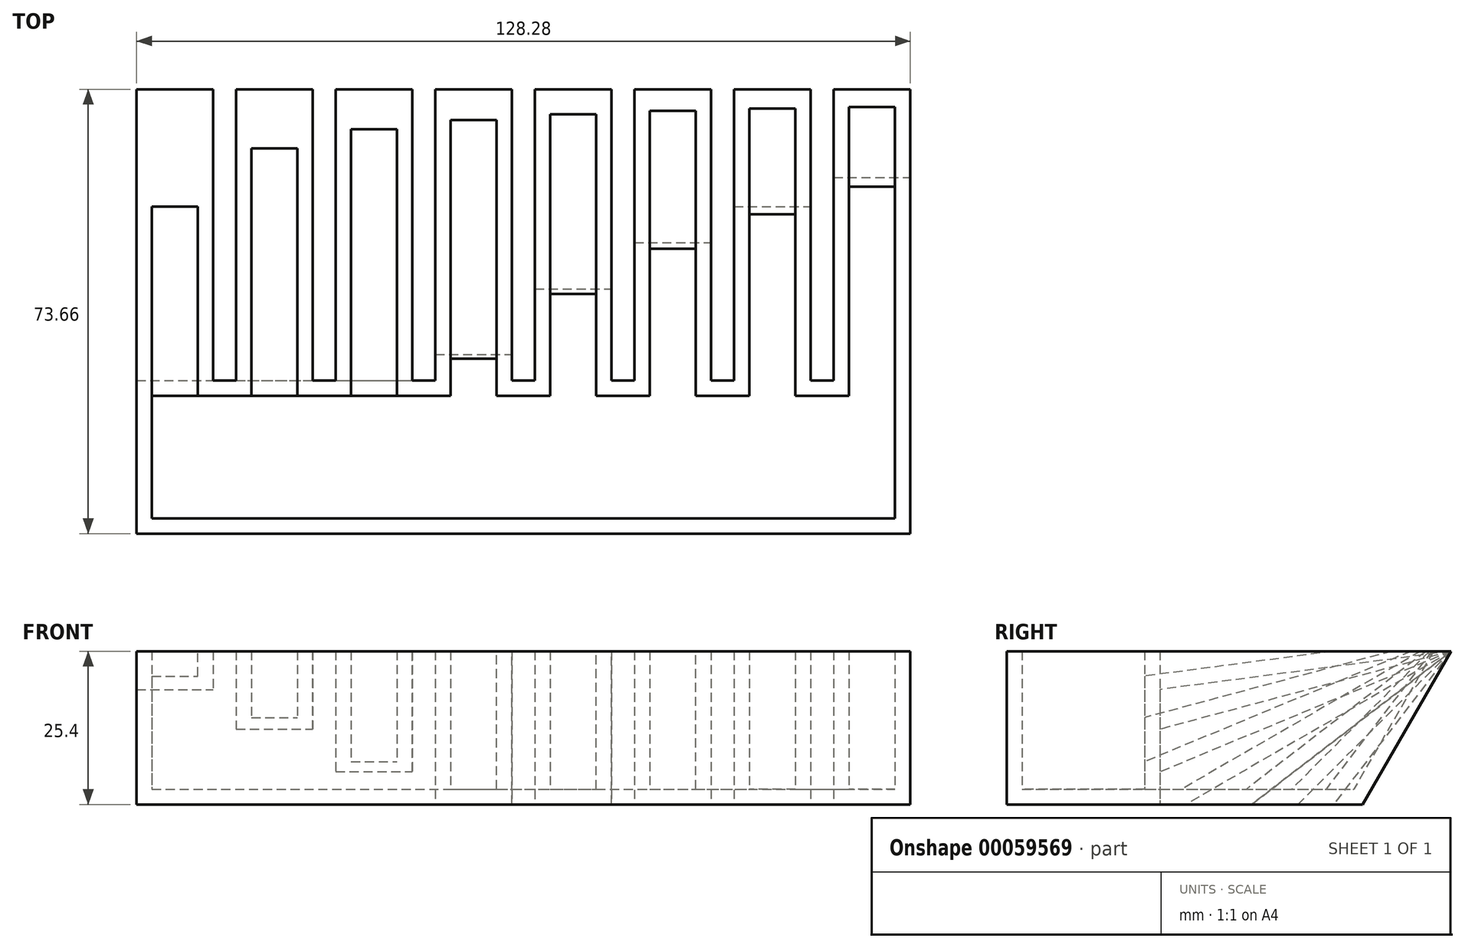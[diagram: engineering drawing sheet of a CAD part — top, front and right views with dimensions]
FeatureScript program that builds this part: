
annotation { "Feature Type Name" : "Feature", "Feature Type Description" : "" }
export const myFeature = defineFeature(function(context is Context, id is Id, definition is map)
    precondition{}
    {
        {
            var Q0;
            Q0=qCreatedBy(makeId("Top.planeOp"),FACE);
            var sketch = newSketch(context, id + "F0", { "sketchPlane" : qUnion([Q0])});
            skLineSegment(sketch, "E0.bottom", {"start": v(-97.16, 0) * mm, "end": v(-84.46, 0) * mm});
            skLineSegment(sketch, "E0.top", {"start": v(-97.16, 50.8) * mm, "end": v(-84.46, 50.8) * mm});
            skLineSegment(sketch, "E0.left", {"start": v(-97.16, 0) * mm, "end": v(-97.16, 50.8) * mm});
            skLineSegment(sketch, "E0.right", {"start": v(-84.46, 0) * mm, "end": v(-84.46, 50.8) * mm});
            skLineSegment(sketch, "E1.bottom", {"start": v(-64.14, 0) * mm, "end": v(-51.44, 0) * mm});
            skLineSegment(sketch, "E1.top", {"start": v(-64.14, 50.8) * mm, "end": v(-51.44, 50.8) * mm});
            skLineSegment(sketch, "E1.left", {"start": v(-64.14, 0) * mm, "end": v(-64.14, 50.8) * mm});
            skLineSegment(sketch, "E1.right", {"start": v(-51.44, 0) * mm, "end": v(-51.44, 50.8) * mm});
            skLineSegment(sketch, "E2.bottom", {"start": v(-47.63, 0) * mm, "end": v(-34.93, 0) * mm});
            skLineSegment(sketch, "E2.top", {"start": v(-47.63, 50.8) * mm, "end": v(-34.93, 50.8) * mm});
            skLineSegment(sketch, "E2.left", {"start": v(-47.63, 0) * mm, "end": v(-47.63, 50.8) * mm});
            skLineSegment(sketch, "E2.right", {"start": v(-34.93, 0) * mm, "end": v(-34.93, 50.8) * mm});
            skLineSegment(sketch, "E3.bottom", {"start": v(-80.65, 0) * mm, "end": v(-67.95, 0) * mm});
            skLineSegment(sketch, "E3.top", {"start": v(-80.65, 50.8) * mm, "end": v(-67.95, 50.8) * mm});
            skLineSegment(sketch, "E3.left", {"start": v(-80.65, 0) * mm, "end": v(-80.65, 50.8) * mm});
            skLineSegment(sketch, "E3.right", {"start": v(-67.95, 0) * mm, "end": v(-67.95, 50.8) * mm});
            skLineSegment(sketch, "E4.bottom", {"start": v(-31.12, 0) * mm, "end": v(-18.42, 0) * mm});
            skLineSegment(sketch, "E4.top", {"start": v(-31.12, 50.8) * mm, "end": v(-18.42, 50.8) * mm});
            skLineSegment(sketch, "E4.left", {"start": v(-31.12, 0) * mm, "end": v(-31.12, 50.8) * mm});
            skLineSegment(sketch, "E4.right", {"start": v(-18.42, 0) * mm, "end": v(-18.42, 50.8) * mm});
            skLineSegment(sketch, "E5.bottom", {"start": v(-14.6, 0) * mm, "end": v(-1.9, 0) * mm});
            skLineSegment(sketch, "E5.top", {"start": v(-14.6, 50.8) * mm, "end": v(-1.9, 50.8) * mm});
            skLineSegment(sketch, "E5.left", {"start": v(-14.6, 0) * mm, "end": v(-14.6, 50.8) * mm});
            skLineSegment(sketch, "E5.right", {"start": v(-1.9, 0) * mm, "end": v(-1.9, 50.8) * mm});
            skLineSegment(sketch, "E6.MirrorCS", {"start": v(31.12, 0) * mm, "end": v(31.12, 50.8) * mm});
            skLineSegment(sketch, "E7.MirrorCS", {"start": v(18.42, 0) * mm, "end": v(18.42, 50.8) * mm});
            skLineSegment(sketch, "E8.MirrorCS", {"start": v(14.6, 0) * mm, "end": v(14.6, 50.8) * mm});
            skLineSegment(sketch, "E9.MirrorCS", {"start": v(1.9, 0) * mm, "end": v(1.9, 50.8) * mm});
            skLineSegment(sketch, "E10.MirrorCS", {"start": v(14.6, 0) * mm, "end": v(1.9, 0) * mm});
            skLineSegment(sketch, "E11.MirrorCS", {"start": v(31.12, 0) * mm, "end": v(18.42, 0) * mm});
            skLineSegment(sketch, "E12.MirrorCS", {"start": v(31.12, 50.8) * mm, "end": v(18.42, 50.8) * mm});
            skLineSegment(sketch, "E13.MirrorCS", {"start": v(14.6, 50.8) * mm, "end": v(1.9, 50.8) * mm});
            skSolve(sketch);
        }
        {
            var Q0;
            Q0=makeQuery(id+"F0.imprint","IMPRINT",FACE,{"disambiguationData":[TD([[makeQuery(id+"F0.imprint","IMPRINT",EDGE,{"derivedFrom":sQuery(id+"F0.wireOp",EDGE,"E0.bottom")}),1.0]])]});
            var Q1;
            Q1=makeQuery(id+"F0.imprint","IMPRINT",FACE,{"disambiguationData":[TD([[makeQuery(id+"F0.imprint","IMPRINT",EDGE,{"derivedFrom":sQuery(id+"F0.wireOp",EDGE,"E3.bottom")}),1.0]])]});
            var Q2;
            Q2=makeQuery(id+"F0.imprint","IMPRINT",FACE,{"disambiguationData":[TD([[makeQuery(id+"F0.imprint","IMPRINT",EDGE,{"derivedFrom":sQuery(id+"F0.wireOp",EDGE,"E1.bottom")}),1.0]])]});
            var Q3;
            Q3=makeQuery(id+"F0.imprint","IMPRINT",FACE,{"disambiguationData":[TD([[makeQuery(id+"F0.imprint","IMPRINT",EDGE,{"derivedFrom":sQuery(id+"F0.wireOp",EDGE,"E2.bottom")}),1.0]])]});
            var Q4;
            Q4=makeQuery(id+"F0.imprint","IMPRINT",FACE,{"disambiguationData":[TD([[makeQuery(id+"F0.imprint","IMPRINT",EDGE,{"derivedFrom":sQuery(id+"F0.wireOp",EDGE,"E4.bottom")}),1.0]])]});
            var Q5;
            Q5=makeQuery(id+"F0.imprint","IMPRINT",FACE,{"disambiguationData":[TD([[makeQuery(id+"F0.imprint","IMPRINT",EDGE,{"derivedFrom":sQuery(id+"F0.wireOp",EDGE,"E5.bottom")}),1.0]])]});
            var Q6;
            Q6=makeQuery(id+"F0.imprint","IMPRINT",FACE,{"disambiguationData":[TD([[makeQuery(id+"F0.imprint","IMPRINT",EDGE,{"derivedFrom":sQuery(id+"F0.wireOp",EDGE,"E8.MirrorCS")}),1.0]])]});
            var Q7;
            Q7=makeQuery(id+"F0.imprint","IMPRINT",FACE,{"disambiguationData":[TD([[makeQuery(id+"F0.imprint","IMPRINT",EDGE,{"derivedFrom":sQuery(id+"F0.wireOp",EDGE,"E6.MirrorCS")}),1.0]])]});
            var Q8;
            Q8=makeQuery(id+"F0.imprint","IMPRINT",FACE,{"disambiguationData":[TD([[makeQuery(id+"F0.imprint","IMPRINT",EDGE,{"derivedFrom":sQuery(id+"F0.wireOp",EDGE,"c19ff177-619e-41c1-baba-1ab0cc4251760.MirrorCS")}),1.0]])]});
            var Q9;
            Q9=makeQuery(id+"F0.imprint","IMPRINT",FACE,{"disambiguationData":[TD([[makeQuery(id+"F0.imprint","IMPRINT",EDGE,{"derivedFrom":sQuery(id+"F0.wireOp",EDGE,"cd565e26-b1c7-4797-8e50-3720e60893980.MirrorCS")}),-1.0]])]});
            var Q10;
            Q10=makeQuery(id+"F0.imprint","IMPRINT",FACE,{"disambiguationData":[TD([[makeQuery(id+"F0.imprint","IMPRINT",EDGE,{"derivedFrom":sQuery(id+"F0.wireOp",EDGE,"f834d962-6a61-4322-8373-423d23230d6e0.MirrorCS")}),1.0]])]});
            var Q11;
            Q11=makeQuery(id+"F0.imprint","IMPRINT",FACE,{"disambiguationData":[TD([[makeQuery(id+"F0.imprint","IMPRINT",EDGE,{"derivedFrom":sQuery(id+"F0.wireOp",EDGE,"851a8a81-0ea1-476b-88e9-f5545ef320b30.MirrorCS")}),-1.0]])]});
            extrude(context, id + "F1", {"entities" : qUnion([Q0, Q1, Q2, Q3, Q4, Q5, Q6, Q7, Q8, Q9, Q10, Q11]), "depth" : 25.4 * mm});
        }
        {
            var Q0;
            Q0=makeQuery(id+"F1.opExtrude","CAP_EDGE",EDGE,{"disambiguationData":[OSD([sQuery(id+"F0.wireOp",EDGE,"E0.top")])],"isStart":true});
            chamfer(context, id + "F2", {"entities" : qUnion([Q0]), "chamferType" : ChamferType.OFFSET_ANGLE, "width" : 192.94 * mm, "oppositeDirection" : false, "angle" : 7.5 * degree, "tangentPropagation" : true});
        }
        {
            var Q0;
            Q0=makeQuery(id+"F1.opExtrude","CAP_EDGE",EDGE,{"disambiguationData":[OSD([sQuery(id+"F0.wireOp",EDGE,"E3.top")])],"isStart":true});
            chamfer(context, id + "F3", {"entities" : qUnion([Q0]), "chamferType" : ChamferType.OFFSET_ANGLE, "width" : 94.8 * mm, "oppositeDirection" : false, "angle" : 15 * degree, "tangentPropagation" : true});
        }
        {
            var Q0;
            Q0=makeQuery(id+"F1.opExtrude","CAP_EDGE",EDGE,{"disambiguationData":[OSD([sQuery(id+"F0.wireOp",EDGE,"E1.top")])],"isStart":true});
            chamfer(context, id + "F4", {"entities" : qUnion([Q0]), "chamferType" : ChamferType.OFFSET_ANGLE, "width" : 61.32 * mm, "oppositeDirection" : false, "angle" : 22.5 * degree, "tangentPropagation" : true});
        }
        {
            var Q0;
            Q0=makeQuery(id+"F1.opExtrude","CAP_EDGE",EDGE,{"disambiguationData":[OSD([sQuery(id+"F0.wireOp",EDGE,"E2.top")])],"isStart":true});
            chamfer(context, id + "F5", {"entities" : qUnion([Q0]), "chamferType" : ChamferType.OFFSET_ANGLE, "width" : 44 * mm, "oppositeDirection" : false, "angle" : 30 * degree, "tangentPropagation" : true});
        }
        {
            var Q0;
            Q0=makeQuery(id+"F1.opExtrude","CAP_EDGE",EDGE,{"disambiguationData":[OSD([sQuery(id+"F0.wireOp",EDGE,"E4.top")])],"isStart":true});
            chamfer(context, id + "F6", {"entities" : qUnion([Q0]), "chamferType" : ChamferType.OFFSET_ANGLE, "width" : 33.1 * mm, "oppositeDirection" : false, "angle" : 37.5 * degree, "tangentPropagation" : true});
        }
        {
            var Q0;
            Q0=makeQuery(id+"F1.opExtrude","CAP_EDGE",EDGE,{"disambiguationData":[OSD([sQuery(id+"F0.wireOp",EDGE,"E5.top")])],"isStart":true});
            chamfer(context, id + "F7", {"entities" : qUnion([Q0]), "chamferType" : ChamferType.OFFSET_ANGLE, "width" : 25.4 * mm, "oppositeDirection" : false, "angle" : 45 * degree, "tangentPropagation" : true});
        }
        {
            var Q0;
            Q0=makeQuery(id+"F1.opExtrude","CAP_EDGE",EDGE,{"disambiguationData":[OSD([sQuery(id+"F0.wireOp",EDGE,"E13.MirrorCS")])],"isStart":true});
            chamfer(context, id + "F8", {"entities" : qUnion([Q0]), "chamferType" : ChamferType.OFFSET_ANGLE, "width" : 25.4 * mm, "oppositeDirection" : false, "angle" : 37.5 * degree, "tangentPropagation" : true});
        }
        {
            var Q0;
            Q0=makeQuery(id+"F1.opExtrude","CAP_EDGE",EDGE,{"disambiguationData":[OSD([sQuery(id+"F0.wireOp",EDGE,"E12.MirrorCS")])],"isStart":true});
            chamfer(context, id + "F9", {"entities" : qUnion([Q0]), "chamferType" : ChamferType.OFFSET_ANGLE, "width" : 25.4 * mm, "oppositeDirection" : false, "angle" : 30 * degree, "tangentPropagation" : true});
        }
        {
            var Q0;
            Q0=qCreatedBy(makeId("Top.planeOp"),FACE);
            var sketch = newSketch(context, id + "F10", { "sketchPlane" : qUnion([Q0])});
            skLineSegment(sketch, "E14.bottom", {"start": v(-97.15, 2.54) * mm, "end": v(31.12, 2.54) * mm});
            skLineSegment(sketch, "E14.top", {"start": v(-97.15, -22.86) * mm, "end": v(31.12, -22.86) * mm});
            skLineSegment(sketch, "E14.left", {"start": v(-97.15, 2.54) * mm, "end": v(-97.15, -22.86) * mm});
            skLineSegment(sketch, "E14.right", {"start": v(31.12, 2.54) * mm, "end": v(31.12, -22.86) * mm});
            skPoint(sketch, "E15.start.orphan", {"position": v(-33.02, -22.86) * mm});
            skSolve(sketch);
        }
        {
            var Q0;
            Q0=makeQuery(id+"F10.imprint","IMPRINT",FACE,{"disambiguationData":[TD([[makeQuery(id+"F10.imprint","IMPRINT",EDGE,{"derivedFrom":sQuery(id+"F10.wireOp",EDGE,"E14.bottom")}),-1.0]])]});
            extrude(context, id + "F11", {"entities" : qUnion([Q0]), "operationType" : NewBodyOperationType.ADD, "depth" : 25.4 * mm});
        }
        {
            var Q0;
            Q0=makeQuery(id+"F11.boolean.opBoolean","MERGE",FACE,{"derivedFrom":[makeQuery(id+"F1.opExtrude","CAP_FACE",FACE,{"disambiguationData":[OSD([sQuery(id+"F0.wireOp",EDGE,"E1.bottom"),sQuery(id+"F0.wireOp",EDGE,"E1.top"),sQuery(id+"F0.wireOp",EDGE,"E1.left"),sQuery(id+"F0.wireOp",EDGE,"E1.right")])],"isStart":false}),makeQuery(id+"F1.opExtrude","CAP_FACE",FACE,{"disambiguationData":[OSD([sQuery(id+"F0.wireOp",EDGE,"E2.bottom"),sQuery(id+"F0.wireOp",EDGE,"E2.top"),sQuery(id+"F0.wireOp",EDGE,"E2.left"),sQuery(id+"F0.wireOp",EDGE,"E2.right")])],"isStart":false}),makeQuery(id+"F1.opExtrude","CAP_FACE",FACE,{"disambiguationData":[OSD([sQuery(id+"F0.wireOp",EDGE,"E3.bottom"),sQuery(id+"F0.wireOp",EDGE,"E3.top"),sQuery(id+"F0.wireOp",EDGE,"E3.left"),sQuery(id+"F0.wireOp",EDGE,"E3.right")])],"isStart":false}),makeQuery(id+"F1.opExtrude","CAP_FACE",FACE,{"disambiguationData":[OSD([sQuery(id+"F0.wireOp",EDGE,"E4.bottom"),sQuery(id+"F0.wireOp",EDGE,"E4.top"),sQuery(id+"F0.wireOp",EDGE,"E4.left"),sQuery(id+"F0.wireOp",EDGE,"E4.right")])],"isStart":false}),makeQuery(id+"F1.opExtrude","CAP_FACE",FACE,{"disambiguationData":[OSD([sQuery(id+"F0.wireOp",EDGE,"E5.bottom"),sQuery(id+"F0.wireOp",EDGE,"E5.top"),sQuery(id+"F0.wireOp",EDGE,"E5.left"),sQuery(id+"F0.wireOp",EDGE,"E5.right")])],"isStart":false}),makeQuery(id+"F1.opExtrude","CAP_FACE",FACE,{"disambiguationData":[OSD([sQuery(id+"F0.wireOp",EDGE,"cd565e26-b1c7-4797-8e50-3720e60893980.MirrorCS"),sQuery(id+"F0.wireOp",EDGE,"9d3064da-bae2-45b4-9700-95b410362f340.MirrorCS"),sQuery(id+"F0.wireOp",EDGE,"2c093ff5-e38e-4e6b-805d-5ac065703b640.MirrorCS"),sQuery(id+"F0.wireOp",EDGE,"c8e67260-9b63-45b2-a96e-6140a1e5b8520.MirrorCS")])],"isStart":false}),makeQuery(id+"F1.opExtrude","CAP_FACE",FACE,{"disambiguationData":[OSD([sQuery(id+"F0.wireOp",EDGE,"c19ff177-619e-41c1-baba-1ab0cc4251760.MirrorCS"),sQuery(id+"F0.wireOp",EDGE,"edb2ae44-dfd0-438d-9011-fcfcb738fec00.MirrorCS"),sQuery(id+"F0.wireOp",EDGE,"91fa4f69-d6ec-41a8-b3b4-15e805d021af0.MirrorCS"),sQuery(id+"F0.wireOp",EDGE,"9a140606-8439-4793-9d1a-0ec345cc02ee0.MirrorCS")])],"isStart":false}),makeQuery(id+"F1.opExtrude","CAP_FACE",FACE,{"disambiguationData":[OSD([sQuery(id+"F0.wireOp",EDGE,"E6.MirrorCS"),sQuery(id+"F0.wireOp",EDGE,"E7.MirrorCS"),sQuery(id+"F0.wireOp",EDGE,"E11.MirrorCS"),sQuery(id+"F0.wireOp",EDGE,"E12.MirrorCS")])],"isStart":false}),makeQuery(id+"F1.opExtrude","CAP_FACE",FACE,{"disambiguationData":[OSD([sQuery(id+"F0.wireOp",EDGE,"E8.MirrorCS"),sQuery(id+"F0.wireOp",EDGE,"E9.MirrorCS"),sQuery(id+"F0.wireOp",EDGE,"E10.MirrorCS"),sQuery(id+"F0.wireOp",EDGE,"E13.MirrorCS")])],"isStart":false}),makeQuery(id+"F1.opExtrude","CAP_FACE",FACE,{"disambiguationData":[OSD([sQuery(id+"F0.wireOp",EDGE,"851a8a81-0ea1-476b-88e9-f5545ef320b30.MirrorCS"),sQuery(id+"F0.wireOp",EDGE,"4ecf547c-3dab-4e7c-bb9c-aba164c54e630.MirrorCS"),sQuery(id+"F0.wireOp",EDGE,"24dc7a96-2908-421f-9e8a-8f084337d24d0.MirrorCS"),sQuery(id+"F0.wireOp",EDGE,"612f31a3-3ace-4dc2-a429-9c291d5c5a0c0.MirrorCS")])],"isStart":false}),makeQuery(id+"F1.opExtrude","CAP_FACE",FACE,{"disambiguationData":[OSD([sQuery(id+"F0.wireOp",EDGE,"f834d962-6a61-4322-8373-423d23230d6e0.MirrorCS"),sQuery(id+"F0.wireOp",EDGE,"c1b5b4fe-f99d-4157-9a91-41b79713ffd00.MirrorCS"),sQuery(id+"F0.wireOp",EDGE,"45098d83-ac12-4ebf-94a3-d277f040351e0.MirrorCS"),sQuery(id+"F0.wireOp",EDGE,"bd2bbc0d-f5b7-4008-81f4-ac5e34f9bea50.MirrorCS")])],"isStart":false}),makeQuery(id+"F1.opExtrude","CAP_FACE",FACE,{"disambiguationData":[OSD([sQuery(id+"F0.wireOp",EDGE,"E0.bottom"),sQuery(id+"F0.wireOp",EDGE,"E0.top"),sQuery(id+"F0.wireOp",EDGE,"E0.left"),sQuery(id+"F0.wireOp",EDGE,"E0.right")])],"isStart":false}),makeQuery(id+"F11.opExtrude","CAP_FACE",FACE,{"disambiguationData":[OSD([sQuery(id+"F10.wireOp",EDGE,"E14.bottom"),sQuery(id+"F10.wireOp",EDGE,"E14.top"),sQuery(id+"F10.wireOp",EDGE,"E14.left"),sQuery(id+"F10.wireOp",EDGE,"E14.right")])],"isStart":false})]});
            shell(context, id + "F12", {"entities" : qUnion([Q0]), "thickness" : 2.54 * mm});
        }
    });
